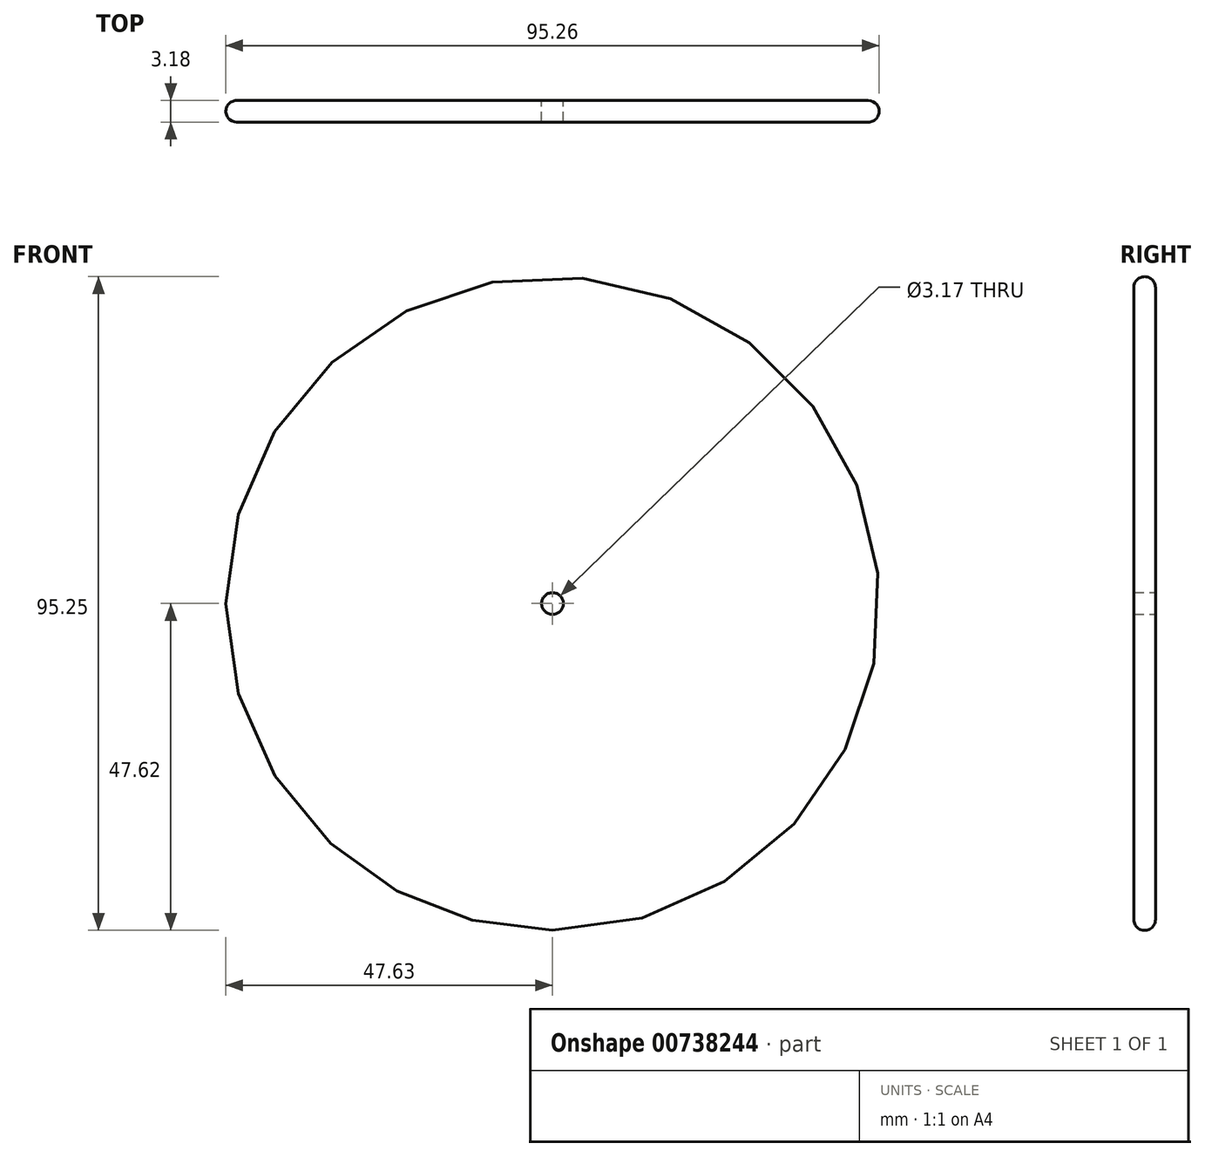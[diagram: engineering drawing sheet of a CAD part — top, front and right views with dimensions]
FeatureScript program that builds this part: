
annotation { "Feature Type Name" : "Feature", "Feature Type Description" : "" }
export const myFeature = defineFeature(function(context is Context, id is Id, definition is map)
    precondition{}
    {
        {
            var Q0;
            Q0=qCreatedBy(makeId("Front.planeOp"),FACE);
            var sketch = newSketch(context, id + "F0", { "sketchPlane" : qUnion([Q0])});
            skCircle(sketch, "E0", {"center": v(0, 0) * mm, "radius": 47.63 * mm});
            skSolve(sketch);
        }
        {
            var Q0;
            Q0=makeQuery(id+"F0.imprint","IMPRINT",FACE,{"disambiguationData":[TD([[makeQuery(id+"F0.imprint","IMPRINT",EDGE,{"derivedFrom":sQuery(id+"F0.wireOp",EDGE,"E0")}),1.0]])]});
            extrude(context, id + "F1", {"entities" : qUnion([Q0]), "depth" : 3.17 * mm, "offsetDistance" : 25.4 * mm});
        }
        {
            var Q0;
            Q0=makeQuery(id+"F1.opExtrude","CAP_EDGE",EDGE,{"disambiguationData":[OSD([sQuery(id+"F0.wireOp",EDGE,"E0")])],"isStart":false});
            var Q1;
            Q1=makeQuery(id+"F1.opExtrude","CAP_EDGE",EDGE,{"disambiguationData":[OSD([sQuery(id+"F0.wireOp",EDGE,"E0")])],"isStart":true});
            fillet(context, id + "F2", {"entities" : qUnion([Q0, Q1]), "radius" : 1.59 * mm, "tangentPropagation" : true, "allowEdgeOverflow" : false});
        }
        {
            var Q0;
            Q0=sQuery(id+"F0.wireOp",VERTEX,"E0.center");
            var Q1;
            Q1=makeQuery(id+"F1.opExtrude","SWEPT_BODY",BODY,{"disambiguationData":[OSD([sQuery(id+"F0.wireOp",EDGE,"E0")])]});
            hole(context, id + "F3", {"style" : HoleStyle.SIMPLE, "endStyle" : HoleEndStyle.THROUGH, "oppositeDirection" : true, "holeDiameter" : 3.17 * mm, "majorDiameter" : 6.35 * mm, "isTappedThrough" : true, "tappedDepth" : 12.7 * mm, "tapClearance" : 3, "locations" : qUnion([Q0]), "scope" : qUnion([Q1])});
        }
    });
